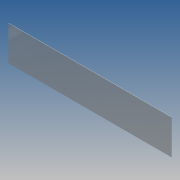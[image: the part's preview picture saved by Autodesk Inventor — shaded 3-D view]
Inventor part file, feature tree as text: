
AUTODESK INVENTOR PART (.ipt)
format: ipt  version: 2013 SP2 (Build 170200200, 200)  size: 134,144 bytes
history: native  units: in
note: dims shown in document units (in); Inventor stores cm internally (conversion verified against a paired STEP export)
features: extrude x1, sketch x1
ambient origin geometry x8: Origin, YZ Plane, XZ Plane, XY Plane, X Axis, Y Axis, Z Axis, Center Point
feature tree (2):
  extrude  "Extrusion2"  Depth=85.0in
  sketch  "Sketch2"  dims[d4=400.0in d5=85.0in d6=1.0in d7=0.0in]
